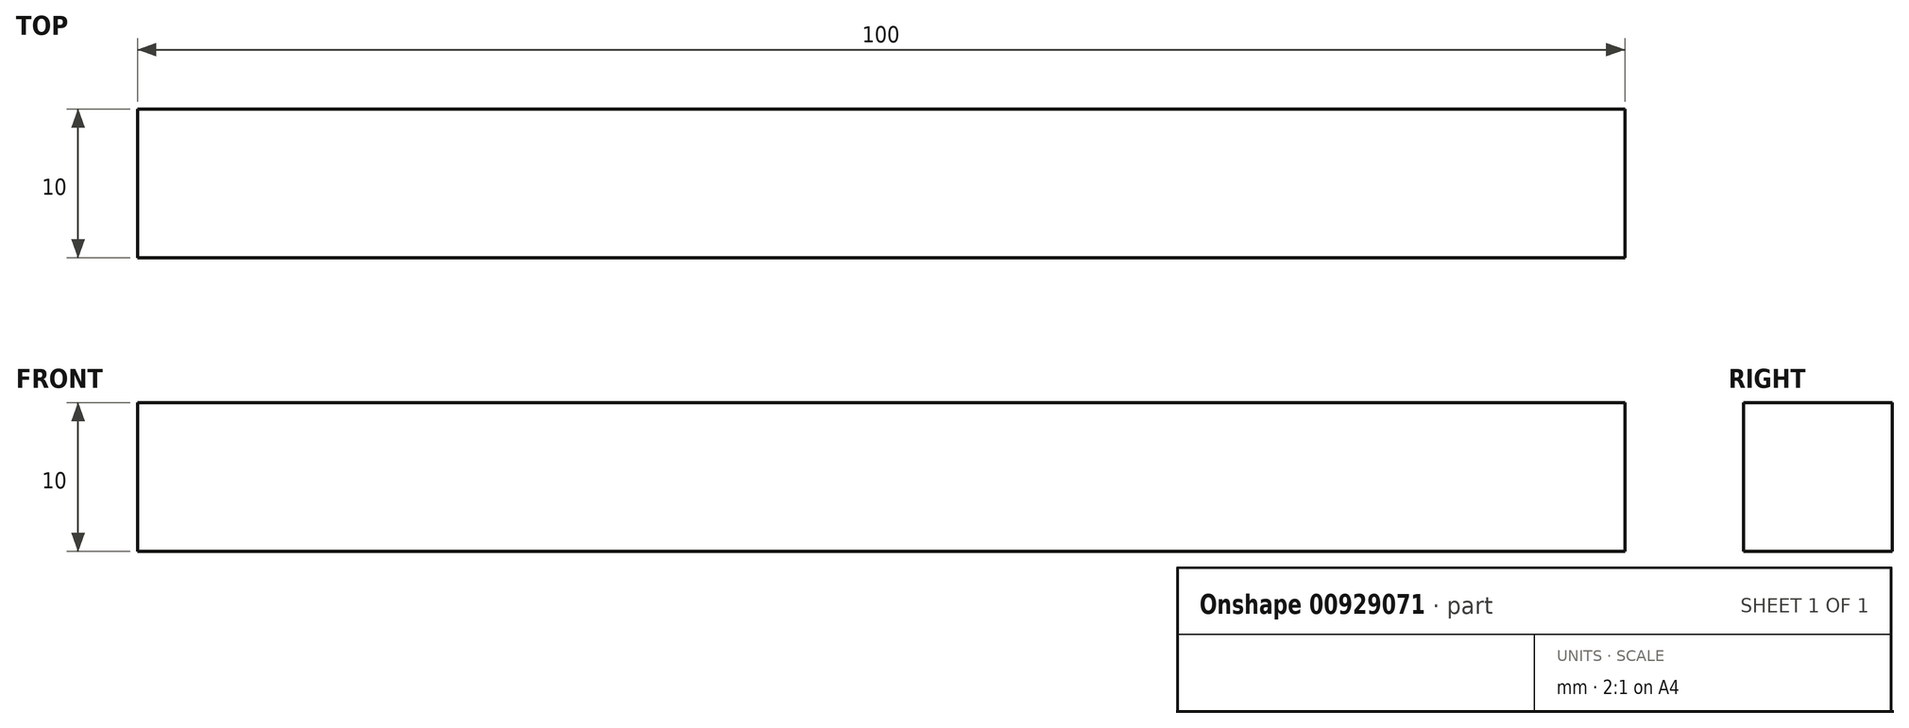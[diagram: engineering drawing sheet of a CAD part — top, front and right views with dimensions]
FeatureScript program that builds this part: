
annotation { "Feature Type Name" : "Feature", "Feature Type Description" : "" }
export const myFeature = defineFeature(function(context is Context, id is Id, definition is map)
    precondition{}
    {
        {
            var Q0;
            Q0=qCreatedBy(makeId("Right.planeOp"),FACE);
            var sketch = newSketch(context, id + "F0", { "sketchPlane" : qUnion([Q0])});
            skLineSegment(sketch, "E0.bottom", {"start": v(5, 5) * mm, "end": v(-5, 5) * mm});
            skLineSegment(sketch, "E0.top", {"start": v(5, -5) * mm, "end": v(-5, -5) * mm});
            skLineSegment(sketch, "E0.left", {"start": v(5, 5) * mm, "end": v(5, -5) * mm});
            skLineSegment(sketch, "E0.right", {"start": v(-5, 5) * mm, "end": v(-5, -5) * mm});
            skPoint(sketch, "E0.middle", {"position": v(0, 0) * mm});
            skSolve(sketch);
        }
        {
            var Q0;
            Q0 = qSketchRegion(id + "F0", true);
            extrude(context, id + "F1", {"entities" : qUnion([Q0]), "endBound" : BoundingType.SYMMETRIC, "depth" : 100 * mm, "offsetDistance" : 25 * mm});
        }
    });
